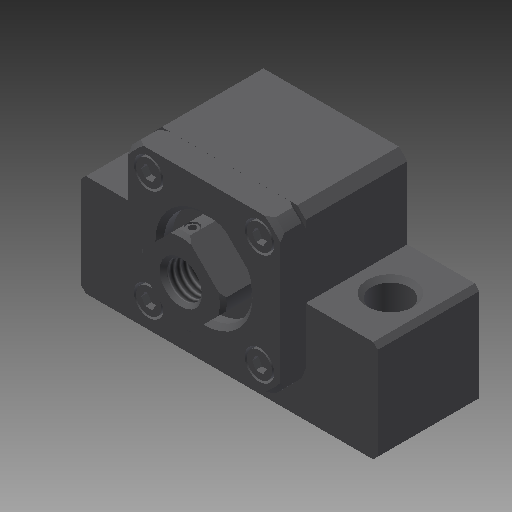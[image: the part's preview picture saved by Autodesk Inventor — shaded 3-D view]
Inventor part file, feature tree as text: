
AUTODESK INVENTOR PART (.ipt)
format: ipt  version: 2018 (Build 220112000, 112)  size: 374,784 bytes
history: native  units: mm
features: sketch x23, revolve x14, other x14, extrude x8, pattern_linear x3, thread x1, hole x1
ambient origin geometry x8: Origin, YZ Plane, XZ Plane, XY Plane, X Axis, Y Axis, Z Axis, Center Point
bodies: Solid1 (feature_tree)
feature tree (64):
  extrude  "Extrusion1"  TaperAngle=360.0deg  [1 undecoded]
  revolve  "Revolution1"  [1 undecoded]
  revolve  "Revolution2"  [1 undecoded]
  extrude  "Extrusion2"  TaperAngle=360.0deg  [1 undecoded]
  revolve  "Revolution3"  [1 undecoded]
  extrude  "Extrusion3"  TaperAngle=360.0deg  [1 undecoded]
  extrude  "Extrusion4"  Depth=20.0mm
  revolve  "Revolution4"  [1 undecoded]
  revolve  "Revolution5"  Angle=360.0deg
  thread  "Thread1"  [1 undecoded]
  revolve  "Revolution6"  [1 undecoded]
  revolve  "Revolution7"  Angle=360.0deg
  extrude  "Extrusion5"  TaperAngle=360.0deg  [1 undecoded]
  pattern_linear  "Rectangular Pattern1"  [2 undecoded]
  pattern_linear  "Rectangular Pattern2"  [2 undecoded]
  pattern_linear  "Rectangular Pattern3"  [2 undecoded]
  revolve  "Revolution8"  [1 undecoded]
  revolve  "Revolution9"  [1 undecoded]
  revolve  "Revolution10"  [1 undecoded]
  revolve  "Revolution11"  [1 undecoded]
  extrude  "Extrusion6"  [1 undecoded]
  hole  "Hole1"  [1 undecoded]
  revolve  "Revolution12"  [1 undecoded]
  extrude  "Extrusion7"  [1 undecoded]
  revolve  "Revolution13"  [1 undecoded]
  revolve  "Revolution14"  [1 undecoded]
  extrude  "Extrusion8"  [1 undecoded]
  other  "unit_XY"
  other  "unit_YZ"
  other  "unit_ZX"
  other  "unit_X"
  other  "unit_Y"
  other  "unit_Z"
  other  "unit_Center"
  other  "unit_collar_XY"
  other  "unit_collar_YZ"
  other  "unit_collar_ZX"
  other  "unit_collar_X"
  other  "unit_collar_Y"
  other  "unit_collar_Z"
  other  "unit_collar_Center"
  sketch  "Sketch_1"  dims[d0=24.0mm d1=0.0mm d2=360.0deg]
  sketch  "Sketch_3"  dims[d3=360.0deg d4=3.0mm d5=0.0mm]
  sketch  "Sketch_4"  dims[d6=360.0deg d7=8.5mm d8=0.0mm]
  sketch  "Sketch_17"  dims[d12=360.0deg d13=6.376mm d14=0.0mm]
  sketch  "Sketch_19"  dims[d25=20.0mm d27=26.162951mm d28=20.0mm d30=26.162951mm d31=20.0mm d33=26.162951mm d34=20.0mm d36=26.162951mm]
  sketch  "Sketch_18"  dims[d15=360.0deg d16=360.0deg]
  sketch  "Sketch_20"  dims[d37=360.0deg d38=360.0deg d39=360.0deg]
  sketch  "Sketch_21"  dims[d40=360.0deg d41=1.2mm d42=0.0mm]
  sketch  "Sketch_22"  dims[d43=10.0mm d44=6.0mm d45=14.5mm d46=6.0mm d47=90.0deg d48=27.5mm d49=0.0mm d50=360.0deg]
  sketch  "Sketch_24"  dims[d51=6.0mm d52=0.0mm d53=360.0deg]
  sketch  "Sketch_25"  dims[d54=360.0deg]
  sketch  "Sketch_28"  dims[d55=0.01mm d56=0.0mm]
  sketch  "Sketch_30"  dims[d57=0.0mm d58=0.0mm]
  sketch  "Sketch_31"
  sketch  "Sketch_32"
  sketch  "Sketch_33"
  sketch  "Sketch_34"
  sketch  "Sketch18"  dims[d17=3.0mm d18=0.0mm d19=20.0mm d21=26.162951mm d22=20.0mm d24=26.162951mm]
  sketch  "Sketch_55"
  sketch  "Sketch_16"  dims[d9=3.0mm d10=0.0mm d11=360.0deg]
  sketch  "Sketch_35"
  sketch  "Sketch_50"
  sketch  "Sketch_51"
note: 27 required parameter values undecoded (feature->parameter linkage not recoverable at this tier; creation-order binding heuristic only, values carry confidence <= 0.55)